# Revit family: Sanitary_Basins_hansgrohe_22473XXX_Avalegra-AquaUnit-780
name_source: partatom
category: Plumbing Fixtures
units: mm (PartAtom-declared; Revit-internal decimal feet)

## family parameters
Always vertical = No
Cut with Voids When Loaded = No
Maintain Annotation Orientation = No
OmniClass Number = 23.31.13.00
OmniClass Title = Sinks
Part Type = Normal
Room Calculation Point = No
Round Connector Dimension = Use Diameter
Shared = No
Work Plane-Based = Yes

## types (5) — shared parameters
CW Connection = No
Connector Description = Water Inlet 9.5 mm
Connector Description 2 = Water Outlet 31.5 mm
Description = Avalegra AquaUnit 780
Diameter = 10 mm  [stored 0.0328084 ft]
Diameter 2 = 32 mm
HW Connection = No
Manufacturer = Hansgrohe
Material 2 = Hansgrohe - Ceramic - White
Model = 22473XXX
Product Page URL = https://www.hansgrohe.com
Product data url = https://bimobject.com
URL = https://www.hansgrohe.com
Vent Connection = No
Version = 1
Waste Connection = No
zero-valued in all types: CWFU, Cost, Default Elevation, HWFU, WFU

## per-type parameters (varying)
| type | Material 1 |
| 340 Brushed Black Chrome | Hansgrohe - Metal - 340 Brushed Black Chrome |
| 000 Chrome | Hansgrohe - Metal - 000 Chrome |
| 140 Brushed Bronze | Hansgrohe - Metal - 147 Brushed Bronze |
| 990 Polished Gold Optic | Hansgrohe - Metal - 990 Polished Gold Optic |
| 670 Matt Black | Hansgrohe - Metal - 670 Matt Black |

note: [stored X ft] marks values corroborated as IEEE doubles in the binary element streams (Revit-internal decimal feet)

## geometry (parser evidence)
native form markers: Sweep x3
no freeform markers — native parametric forms only
